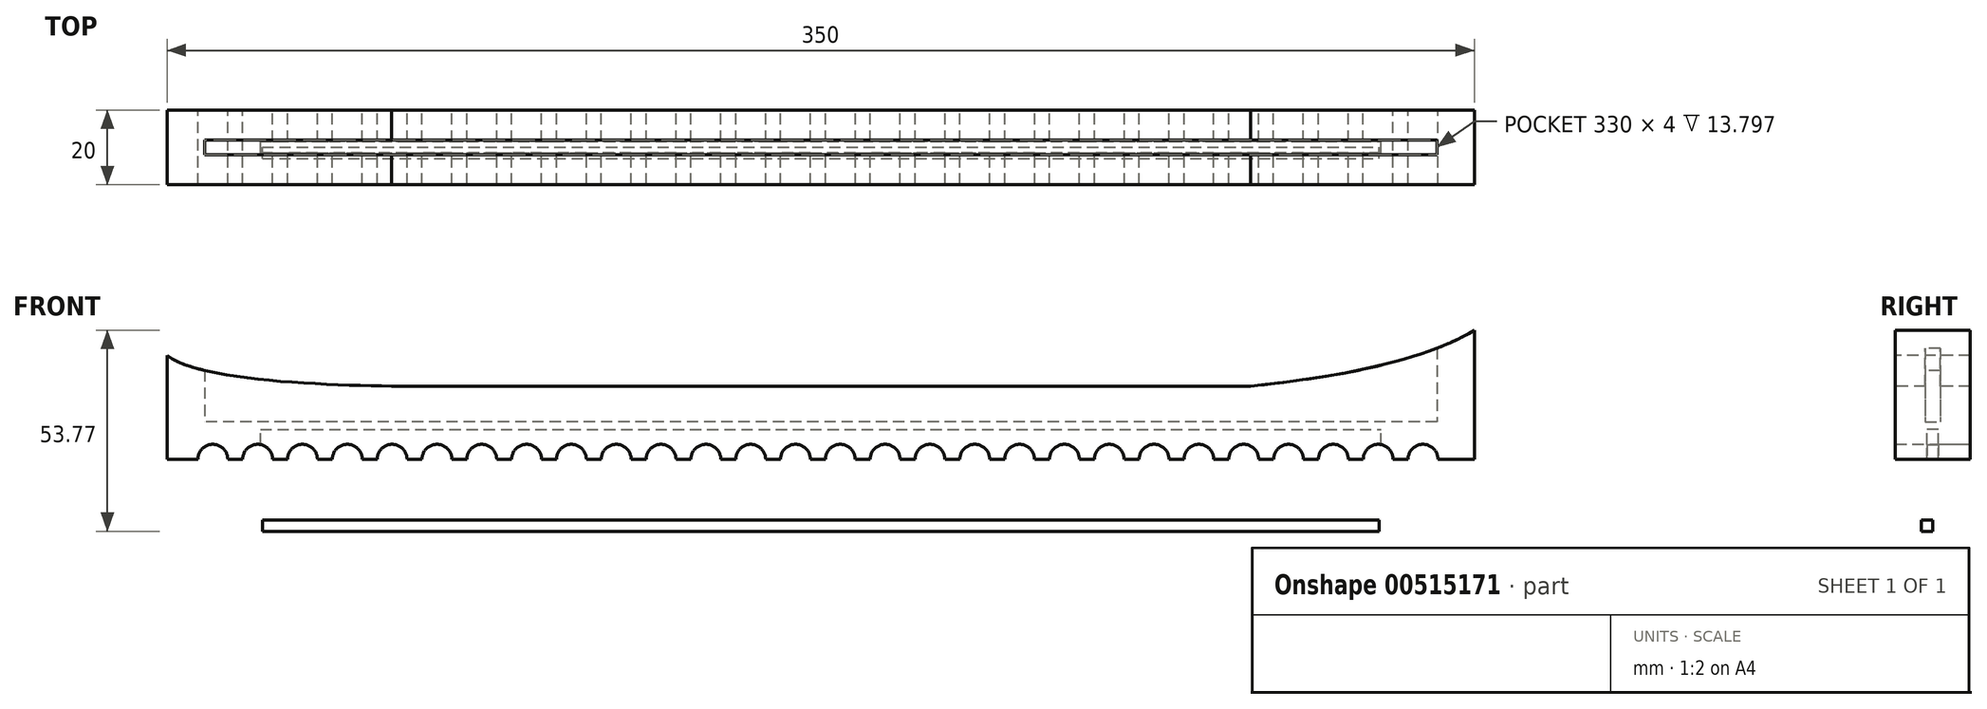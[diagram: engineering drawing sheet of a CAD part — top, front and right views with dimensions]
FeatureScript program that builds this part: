
annotation { "Feature Type Name" : "Feature", "Feature Type Description" : "" }
export const myFeature = defineFeature(function(context is Context, id is Id, definition is map)
    precondition{}
    {
        {
            var Q0;
            Q0=qCreatedBy(makeId("Top.planeOp"),FACE);
            var sketch = newSketch(context, id + "F0", { "sketchPlane" : qUnion([Q0])});
            skLineSegment(sketch, "E0.bottom", {"start": v(175, -10) * mm, "end": v(-175, -10) * mm});
            skLineSegment(sketch, "E0.top", {"start": v(175, 10) * mm, "end": v(-175, 10) * mm});
            skLineSegment(sketch, "E0.left", {"start": v(175, -10) * mm, "end": v(175, 10) * mm});
            skLineSegment(sketch, "E0.right", {"start": v(-175, -10) * mm, "end": v(-175, 10) * mm});
            skPoint(sketch, "E0.middle", {"position": v(0, 0) * mm});
            skLineSegment(sketch, "E1.bottom", {"start": v(165, -2) * mm, "end": v(-165, -2) * mm});
            skLineSegment(sketch, "E1.top", {"start": v(165, 2) * mm, "end": v(-165, 2) * mm});
            skLineSegment(sketch, "E1.left", {"start": v(165, -2) * mm, "end": v(165, 2) * mm});
            skLineSegment(sketch, "E1.right", {"start": v(-165, -2) * mm, "end": v(-165, 2) * mm});
            skSolve(sketch);
        }
        {
            var Q0;
            Q0=makeQuery(id+"F0.imprint","IMPRINT",FACE,{"disambiguationData":[TD([[makeQuery(id+"F0.imprint","IMPRINT",EDGE,{"derivedFrom":sQuery(id+"F0.wireOp",EDGE,"E0.bottom")}),-1.0]])]});
            var Q1;
            Q1=makeQuery(id+"F0.imprint","IMPRINT",FACE,{"disambiguationData":[TD([[makeQuery(id+"F0.imprint","IMPRINT",EDGE,{"derivedFrom":sQuery(id+"F0.wireOp",EDGE,"E1.bottom")}),-1.0]])]});
            extrude(context, id + "F1", {"entities" : qUnion([Q0, Q1]), "oppositeDirection" : true, "depth" : 10 * mm, "offsetDistance" : 25 * mm});
        }
        {
            var Q0;
            Q0 = qSketchRegion(id + "F0", true);
            extrude(context, id + "F2", {"entities" : qUnion([Q0]), "operationType" : NewBodyOperationType.ADD, "depth" : 25 * mm, "offsetDistance" : 25 * mm});
        }
        {
            var Q0;
            Q0=qCreatedBy(makeId("Front.planeOp"),FACE);
            var sketch = newSketch(context, id + "F3", { "sketchPlane" : qUnion([Q0])});
            skCircle(sketch, "E2", {"center": v(-162.75, -9.98) * mm, "radius": 4 * mm});
            skCircle(sketch, "E3.1.0.0", {"center": v(-150.75, -9.98) * mm, "radius": 4 * mm});
            skCircle(sketch, "E3.2.0.0", {"center": v(-138.75, -9.98) * mm, "radius": 4 * mm});
            skCircle(sketch, "E3.3.0.0", {"center": v(-126.75, -9.98) * mm, "radius": 4 * mm});
            skCircle(sketch, "E3.4.0.0", {"center": v(-114.75, -9.98) * mm, "radius": 4 * mm});
            skCircle(sketch, "E3.5.0.0", {"center": v(-102.75, -9.98) * mm, "radius": 4 * mm});
            skCircle(sketch, "E3.6.0.0", {"center": v(-90.75, -9.98) * mm, "radius": 4 * mm});
            skCircle(sketch, "E3.7.0.0", {"center": v(-78.75, -9.98) * mm, "radius": 4 * mm});
            skCircle(sketch, "E3.8.0.0", {"center": v(-66.75, -9.98) * mm, "radius": 4 * mm});
            skCircle(sketch, "E3.9.0.0", {"center": v(-54.75, -9.98) * mm, "radius": 4 * mm});
            skCircle(sketch, "E3.10.0.0", {"center": v(-42.75, -9.98) * mm, "radius": 4 * mm});
            skCircle(sketch, "E3.11.0.0", {"center": v(-30.75, -9.98) * mm, "radius": 4 * mm});
            skCircle(sketch, "E3.12.0.0", {"center": v(-18.75, -9.98) * mm, "radius": 4 * mm});
            skCircle(sketch, "E3.13.0.0", {"center": v(-6.75, -9.98) * mm, "radius": 4 * mm});
            skCircle(sketch, "E3.14.0.0", {"center": v(5.25, -9.98) * mm, "radius": 4 * mm});
            skCircle(sketch, "E3.15.0.0", {"center": v(17.25, -9.98) * mm, "radius": 4 * mm});
            skCircle(sketch, "E3.16.0.0", {"center": v(29.25, -9.98) * mm, "radius": 4 * mm});
            skCircle(sketch, "E3.17.0.0", {"center": v(41.25, -9.98) * mm, "radius": 4 * mm});
            skCircle(sketch, "E3.18.0.0", {"center": v(53.25, -9.98) * mm, "radius": 4 * mm});
            skCircle(sketch, "E3.19.0.0", {"center": v(65.25, -9.98) * mm, "radius": 4 * mm});
            skCircle(sketch, "E3.20.0.0", {"center": v(77.25, -9.98) * mm, "radius": 4 * mm});
            skCircle(sketch, "E3.21.0.0", {"center": v(89.25, -9.98) * mm, "radius": 4 * mm});
            skCircle(sketch, "E3.22.0.0", {"center": v(101.25, -9.98) * mm, "radius": 4 * mm});
            skCircle(sketch, "E3.23.0.0", {"center": v(113.25, -9.98) * mm, "radius": 4 * mm});
            skCircle(sketch, "E3.24.0.0", {"center": v(125.25, -9.98) * mm, "radius": 4 * mm});
            skCircle(sketch, "E3.25.0.0", {"center": v(137.25, -9.98) * mm, "radius": 4 * mm});
            skCircle(sketch, "E3.26.0.0", {"center": v(149.25, -9.98) * mm, "radius": 4 * mm});
            skCircle(sketch, "E3.27.0.0", {"center": v(161.25, -9.98) * mm, "radius": 4 * mm});
            skLineSegment(sketch, "E3.direction1", {"start": v(-162.75, -9.98) * mm, "end": v(-150.75, -9.98) * mm, "construction": true});
            skSolve(sketch);
        }
        {
            var Q0;
            Q0 = qSketchRegion(id + "F3", true);
            extrude(context, id + "F4", {"entities" : qUnion([Q0]), "operationType" : NewBodyOperationType.REMOVE, "endBound" : BoundingType.SYMMETRIC, "depth" : 25 * mm, "offsetDistance" : 25 * mm});
        }
        {
            var Q0;
            Q0=qCreatedBy(makeId("Front.planeOp"),FACE);
            var sketch = newSketch(context, id + "F5", { "sketchPlane" : qUnion([Q0])});
            skLineSegment(sketch, "E4", {"start": v(-114.9, 9.6) * mm, "end": v(115.1, 9.6) * mm});
            skFitSpline(sketch, "E5", {"points": [v(-114.9, 9.6) * mm, v(-175.52, 25.93) * mm], "startDerivative": vector(-79.09, 1.1) * mm, "endDerivative": vector(34.94, 41.88) * mm});
            skFitSpline(sketch, "E6", {"points": [v(115.1, 9.6) * mm, v(189.44, 44.02) * mm], "startDerivative": vector(176.06, 17.63) * mm, "endDerivative": vector(5.76, 42.6) * mm});
            skLineSegment(sketch, "E7", {"start": v(-114.9, 9.6) * mm, "end": v(-114.9, 17.6) * mm, "construction": true});
            skLineSegment(sketch, "E8", {"start": v(115.1, 9.6) * mm, "end": v(115.1, 24.6) * mm, "construction": true});
            skLineSegment(sketch, "E9", {"start": v(-114.9, 17.6) * mm, "end": v(-174.9, 17.6) * mm, "construction": true});
            skLineSegment(sketch, "E10", {"start": v(115.1, 24.6) * mm, "end": v(175.1, 24.6) * mm, "construction": true});
            skLineSegment(sketch, "E11", {"start": v(-175.52, 25.93) * mm, "end": v(189.44, 44.02) * mm});
            skSolve(sketch);
        }
        {
            var Q0;
            Q0 = qSketchRegion(id + "F5", true);
            extrude(context, id + "F6", {"entities" : qUnion([Q0]), "operationType" : NewBodyOperationType.REMOVE, "endBound" : BoundingType.SYMMETRIC, "oppositeDirection" : true, "depth" : 25 * mm, "offsetDistance" : 25 * mm});
        }
        {
            var Q0;
            Q0=qCreatedBy(makeId("Front.planeOp"),FACE);
            var sketch = newSketch(context, id + "F7", { "sketchPlane" : qUnion([Q0])});
            skLineSegment(sketch, "E12.bottom", {"start": v(-150, -10) * mm, "end": v(150, -10) * mm});
            skLineSegment(sketch, "E12.top", {"start": v(-150, -2) * mm, "end": v(150, -2) * mm});
            skLineSegment(sketch, "E12.left", {"start": v(-150, -10) * mm, "end": v(-150, -2) * mm});
            skLineSegment(sketch, "E12.right", {"start": v(150, -10) * mm, "end": v(150, -2) * mm});
            skPoint(sketch, "E12.middle", {"position": v(0, -6) * mm});
            skSolve(sketch);
        }
        {
            var Q0;
            Q0 = qSketchRegion(id + "F7", true);
            extrude(context, id + "F8", {"entities" : qUnion([Q0]), "operationType" : NewBodyOperationType.REMOVE, "endBound" : BoundingType.SYMMETRIC, "oppositeDirection" : true, "depth" : 3 * mm, "offsetDistance" : 25 * mm});
        }
        {
            var Q0;
            Q0=qCreatedBy(makeId("Front.planeOp"),FACE);
            var sketch = newSketch(context, id + "F9", { "sketchPlane" : qUnion([Q0])});
            skLineSegment(sketch, "E13.bottom", {"start": v(-149.5, -29.25) * mm, "end": v(149.5, -29.25) * mm});
            skLineSegment(sketch, "E13.top", {"start": v(-149.5, -26.25) * mm, "end": v(149.5, -26.25) * mm});
            skLineSegment(sketch, "E13.left", {"start": v(-149.5, -29.25) * mm, "end": v(-149.5, -26.25) * mm});
            skLineSegment(sketch, "E13.right", {"start": v(149.5, -29.25) * mm, "end": v(149.5, -26.25) * mm});
            skPoint(sketch, "E13.middle", {"position": v(0, -27.75) * mm});
            skSolve(sketch);
        }
        {
            var Q0;
            Q0 = qSketchRegion(id + "F9", true);
            extrude(context, id + "F10", {"entities" : qUnion([Q0]), "depth" : 3 * mm, "offsetDistance" : 25 * mm});
        }
    });
